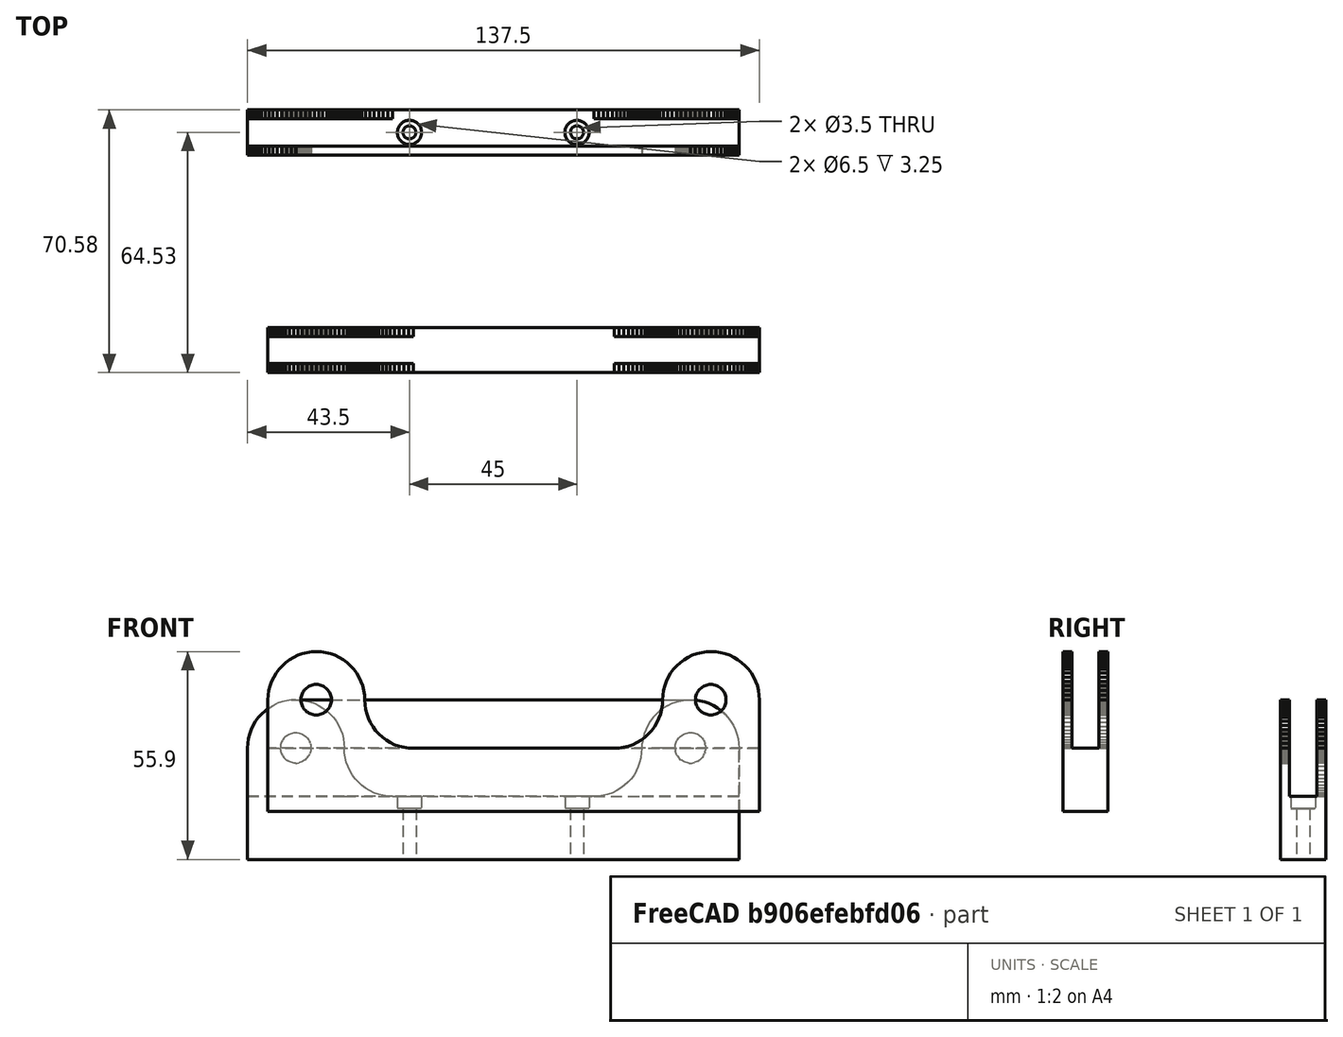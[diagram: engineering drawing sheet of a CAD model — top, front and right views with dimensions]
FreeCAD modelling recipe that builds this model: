
FCSTD DOCUMENT  (FreeCAD 0.20RUnknown)
Label: FilamentSpoolHolderRemix
License: All rights reserved
LicenseURL: http://en.wikipedia.org/wiki/All_rights_reserved
objects: Part::Feature×4, Sketcher::SketchObject×3, Mesh::Feature×2, PartDesign::FeatureBase×2, PartDesign::Pad×2, PartDesign::Body×2, Part::Compound×1, PartDesign::Hole×1
note: 18 computed .brp shape members not serialized (recipe doc carries the construction recipe); baked Part::Feature solids carry a one-line shape summary decoded from their .brp

FEATURE [Mesh::Feature] filament_spool_holder_center
FEATURE [Mesh::Feature] filament_spool_holder_ends
FEATURE [Part::Feature] filament_spool_holder_center001
  shape: bbox 132 x 12.1 x 30 mm, 1896 faces, 0 solids (baked)
FEATURE [Part::Feature] filament_spool_holder_center001_solid  label="filament_spool_holder_center001 (Solid)"
  shape: bbox 132 x 12.1 x 30 mm, 1896 faces (baked)
FEATURE [PartDesign::FeatureBase] BaseFeature
  BaseFeature = -> filament_spool_holder_center001_solid
FEATURE [Sketcher::SketchObject] Sketch
  ExternalGeometry = -> [BaseFeature]
  FullyConstrained = true
  MapMode = 5
  Placement = pos=(0,25,0) rot=(1,0,0;1.5708rad)
  Support = -> [BaseFeature]
  sketch-geometry (17):
    g0: Circle CenterX=-53.05 CenterY=17.0531 CenterZ=0 NormalX=0 NormalY=0 NormalZ=1 AngleXU=0 Radius=4.0997
    g1: Circle CenterX=-53 CenterY=17.0001 CenterZ=0 NormalX=0 NormalY=0 NormalZ=1 AngleXU=0 Radius=12.9996
    g2: Circle CenterX=52.9498 CenterY=17.0495 CenterZ=0 NormalX=0 NormalY=0 NormalZ=1 AngleXU=0 Radius=4.10286
    g3: Circle CenterX=53.0001 CenterY=16.9998 CenterZ=0 NormalX=0 NormalY=0 NormalZ=1 AngleXU=0 Radius=12.9999
    g4: Circle CenterX=-53.05 CenterY=17.0531 CenterZ=0 NormalX=0 NormalY=0 NormalZ=1 AngleXU=0 Radius=11
    g5: Circle CenterX=53.0001 CenterY=16.9998 CenterZ=0 NormalX=0 NormalY=0 NormalZ=1 AngleXU=0 Radius=11
    g6: Circle CenterX=0 CenterY=114.555 CenterZ=0 NormalX=0 NormalY=0 NormalZ=1 AngleXU=0 Radius=100
    g7: LineSegment StartX=-53.05 StartY=17.0531 StartZ=0 EndX=-53.05 EndY=29.9996 EndZ=0
    g8: LineSegment StartX=52.9498 StartY=17.0495 StartZ=0 EndX=52.9498 EndY=29.9996 EndZ=0
    g9: LineSegment StartX=-53.05 StartY=29.9996 StartZ=0 EndX=52.9498 EndY=29.9996 EndZ=0
    g10: LineSegment StartX=-53.05 StartY=29.9996 StartZ=0 EndX=-39.94 EndY=15.726 EndZ=0
    g11: LineSegment StartX=-39.94 StartY=15.726 StartZ=0 EndX=-39.94 EndY=3.998 EndZ=0
    g12: LineSegment StartX=-39.94 StartY=3.998 StartZ=0 EndX=-27.002 EndY=3.998 EndZ=0
    g13: LineSegment StartX=-27.002 StartY=3.998 StartZ=0 EndX=27.001 EndY=3.998 EndZ=0
    g14: LineSegment StartX=27.001 StartY=3.998 StartZ=0 EndX=40.001 EndY=3.998 EndZ=0
    g15: LineSegment StartX=40.001 StartY=3.998 StartZ=0 EndX=40.001 EndY=17.0204 EndZ=0
    g16: LineSegment StartX=40.001 StartY=17.0204 StartZ=0 EndX=52.9498 EndY=29.9996 EndZ=0
  constraints (43):
    c: PointOnObject(g-5,g0)
    c: PointOnObject(g-4,g0)
    c: PointOnObject(g-3,g0)
    c: PointOnObject(g-8,g1)
    c: PointOnObject(g-6,g1)
    c: PointOnObject(g-9,g1)
    c: PointOnObject(g-12,g2)
    c: PointOnObject(g-13,g2)
    c: PointOnObject(g-14,g2)
    c: PointOnObject(g-15,g3)
    c: PointOnObject(g-16,g3)
    c: PointOnObject(g-17,g3)
    c: Coincident(g4,g0)
    c: Coincident(g5,g3)
    c: Equal(g4,g5)
    c: Diameter(g4) = 22
    c: PointOnObject(g6,g-2)
    c: Tangent(g6,g4)
    c: Diameter(g6) = 200
    c: Coincident(g7,g0)
    c: PointOnObject(g7,g1)
    c: Coincident(g8,g2)
    c: PointOnObject(g8,g3)
    c: Vertical(g7)
    c: Vertical(g8)
    c: Coincident(g9,g7)
    c: Coincident(g9,g8)
    c: Coincident(g9,g10)
    c: Coincident(g10,g11)
    c: Vertical(g11)
    c: Coincident(g11,g12)
    c: Coincident(g12,g-11)
    c: Horizontal(g12)
    c: Coincident(g12,g13)
    c: Coincident(g13,g-11)
    c: Coincident(g13,g14)
    c: Horizontal(g14)
    c: Coincident(g14,g15)
    c: Coincident(g15,g-18)
    c: Vertical(g15)
    c: Coincident(g15,g16)
    c: Coincident(g16,g9)
    c: Coincident(g10,g-10)
FEATURE [PartDesign::Pad] Pad
  BaseFeature = -> BaseFeature
  Direction = (0,-1,2e-16)
  Length = 10
  Length2 = 10
  Profile = -> Sketch
  ReferenceAxis = -> Sketch [N_Axis]
  Type = 3
  UpToFace = -> BaseFeature [Face1145]
FEATURE [PartDesign::Body] Body  label="Center"
  BaseFeature = -> filament_spool_holder_center001_solid
  Group = -> [BaseFeature,Sketch,Pad]
  Origin = -> Origin
  Tip = -> Pad
FEATURE [Part::Compound] Compound
  Links = -> [Body]
FEATURE [PartDesign::FeatureBase] BaseFeature001
  BaseFeature = -> Compound
FEATURE [Part::Feature] filament_spool_holder_ends001
  shape: bbox 132 x 12.1 x 42.95 mm, 1860 faces, 0 solids (baked)
FEATURE [Part::Feature] filament_spool_holder_ends001_solid  label="filament_spool_holder_ends001 (Solid)"
  shape: bbox 132 x 12.1 x 42.95 mm, 1860 faces (baked)
FEATURE [Sketcher::SketchObject] Sketch001
  ExternalGeometry = -> [BaseFeature001]
  FullyConstrained = true
  MapMode = 5
  Placement = pos=(0,0,0) rot=(1,0,0;3.14159rad)
  Support = -> [BaseFeature001]
  sketch-geometry (4):
    g0: LineSegment StartX=66 StartY=-25 StartZ=0 EndX=-66 EndY=-25 EndZ=0
    g1: LineSegment StartX=-66 StartY=-25 StartZ=0 EndX=-66 EndY=-37.1 EndZ=0
    g2: LineSegment StartX=-66 StartY=-37.1 StartZ=0 EndX=66 EndY=-37.1 EndZ=0
    g3: LineSegment StartX=66 StartY=-37.1 StartZ=0 EndX=66 EndY=-25 EndZ=0
  constraints (10):
    c: Coincident(g0,g1)
    c: Coincident(g1,g2)
    c: Coincident(g2,g3)
    c: Coincident(g3,g0)
    c: Horizontal(g0)
    c: Horizontal(g2)
    c: Vertical(g1)
    c: Vertical(g3)
    c: Coincident(g0,g-4)
    c: Coincident(g1,g-3)
FEATURE [PartDesign::Pad] Pad001
  BaseFeature = -> BaseFeature001
  Direction = (0,0,-1)
  Length = 12.95
  Length2 = 10
  Profile = -> Sketch001
  ReferenceAxis = -> Sketch001 [N_Axis]
  Type = 0
  expr: Length = 16.95 - 4
FEATURE [Sketcher::SketchObject] Sketch002
  ExternalGeometry = -> [Pad001]
  FullyConstrained = true
  MapMode = 5
  Placement = pos=(0,0,3.998) rot=(0,0,1;0rad)
  Support = -> [Pad001]
  sketch-geometry (6):
    g0: LineSegment StartX=0 StartY=25 StartZ=0 EndX=0 EndY=31.05 EndZ=0
    g1: LineSegment StartX=0 StartY=31.05 StartZ=0 EndX=0 EndY=37.1 EndZ=0
    g2: LineSegment StartX=0 StartY=31.05 StartZ=0 EndX=-22.5 EndY=31.05 EndZ=0
    g3: LineSegment StartX=0 StartY=31.05 StartZ=0 EndX=22.5 EndY=31.05 EndZ=0
    g4: Circle CenterX=-22.5 CenterY=31.05 CenterZ=0 NormalX=0 NormalY=0 NormalZ=1 AngleXU=0 Radius=3.25
    g5: Circle CenterX=22.5 CenterY=31.05 CenterZ=0 NormalX=0 NormalY=0 NormalZ=1 AngleXU=0 Radius=3.25
  constraints (17):
    c: PointOnObject(g0,g-2)
    c: PointOnObject(g0,g-2)
    c: PointOnObject(g0,g-3)
    c: PointOnObject(g1,g-4)
    c: Equal(g1,g0)
    c: Coincident(g0,g1)
    c: PointOnObject(g1,g-2)
    c: Coincident(g2,g0)
    c: Horizontal(g2)
    c: Coincident(g3,g0)
    c: Horizontal(g3)
    c: Equal(g2,g3)
    c: Coincident(g4,g2)
    c: Coincident(g5,g3)
    c: Equal(g4,g5)
    c: Diameter(g4) = 6.5
    c: DistanceX(g4,g5) = 45
FEATURE [PartDesign::Hole] Hole
  BaseFeature = -> Pad001
  CustomThreadClearance = 0
  Depth = 281.463
  DepthType = 1
  Diameter = 3.5
  DrillForDepth = false
  DrillPoint = 1
  DrillPointAngle = 118
  HoleCutCountersinkAngle = 90
  HoleCutCustomValues = false
  HoleCutDepth = 3.25
  HoleCutDiameter = 6.5
  HoleCutType = 1
  ModelThread = false
  Profile = -> Sketch002
  Tapered = false
  TaperedAngle = 90
  ThreadClass = 0
  ThreadDepth = 281.463
  ThreadDepthType = 0
  ThreadDirection = 0
  ThreadFit = 0
  ThreadSize = 0
  ThreadType = 0
  Threaded = false
  UseCustomThreadClearance = false
FEATURE [PartDesign::Body] Body001  label="End"
  BaseFeature = -> Compound
  Group = -> [BaseFeature001,Sketch001,Pad001,Sketch002,Hole]
  Origin = -> Origin001
  Tip = -> Hole
